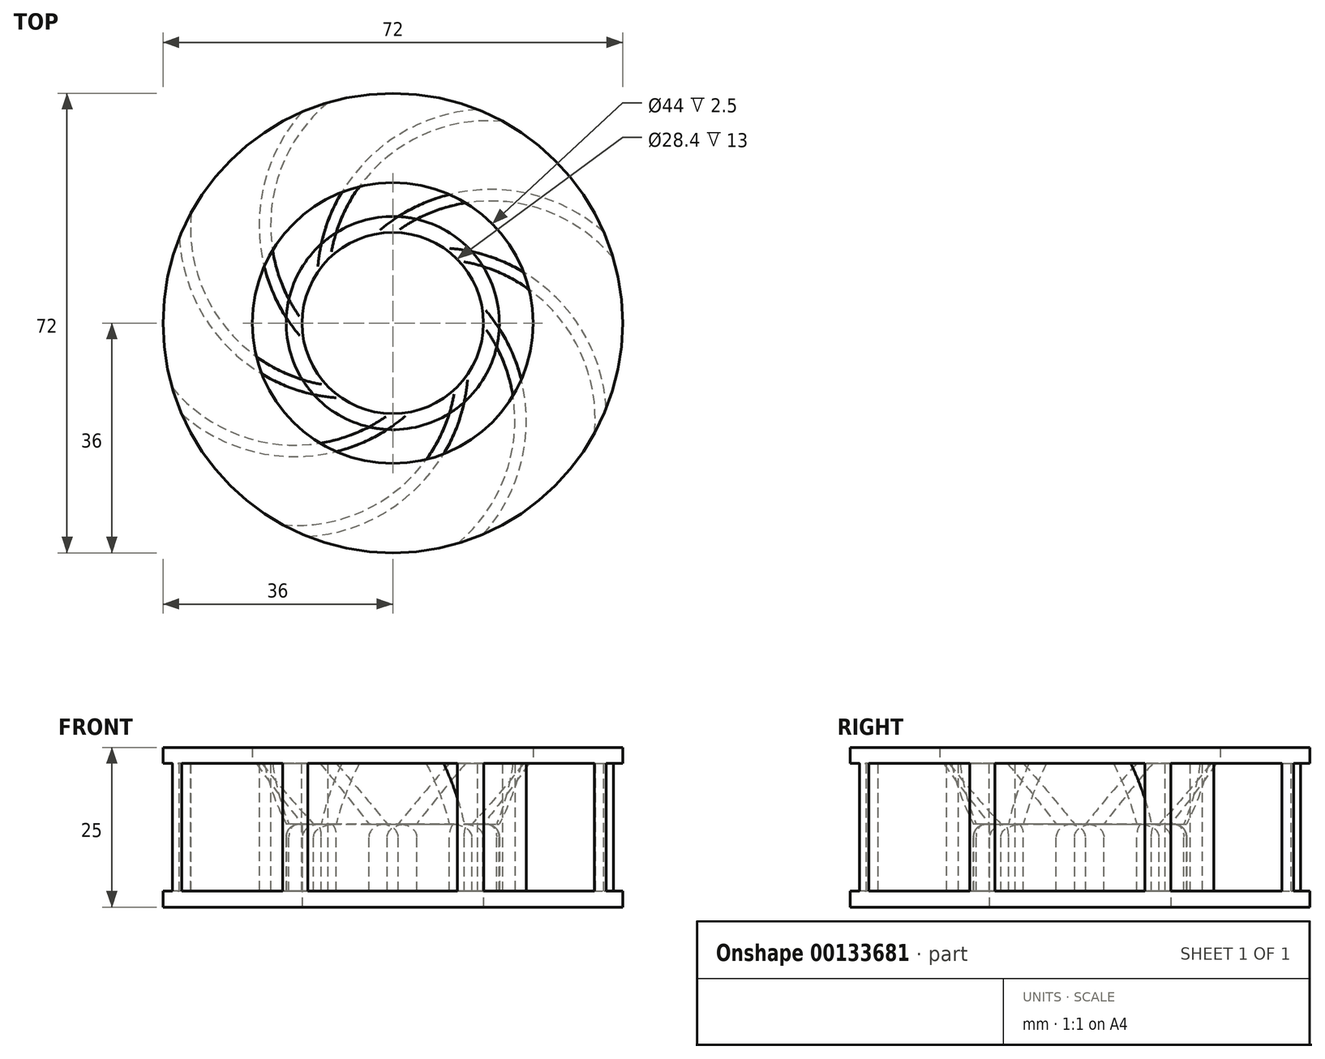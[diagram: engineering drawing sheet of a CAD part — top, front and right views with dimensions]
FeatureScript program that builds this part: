
annotation { "Feature Type Name" : "Feature", "Feature Type Description" : "" }
export const myFeature = defineFeature(function(context is Context, id is Id, definition is map)
    precondition{}
    {
        {
            var Q0;
            Q0=qCreatedBy(makeId("Top.planeOp"),FACE);
            var sketch = newSketch(context, id + "F0", { "sketchPlane" : qUnion([Q0])});
            skCircle(sketch, "E0", {"center": v(0, 0) * mm, "radius": 38 * mm});
            skCircle(sketch, "E1", {"center": v(0, 0) * mm, "radius": 14 * mm, "construction": true});
            skCircle(sketch, "E2", {"center": v(-5, 15) * mm, "radius": 25 * mm});
            skCircle(sketch, "E3", {"center": v(-5, 15) * mm, "radius": 26.8 * mm});
            skLineSegment(sketch, "E4", {"start": v(-5, 15) * mm, "end": v(0, 15) * mm});
            skLineSegment(sketch, "E5", {"start": v(0, 15) * mm, "end": v(0, 0) * mm});
            skLineSegment(sketch, "E6", {"start": v(-2.4, -9.86) * mm, "end": v(5, -9.86) * mm});
            skSolve(sketch);
        }
        {
            var Q0;
            {var subQ0=sQuery(id+"F0.wireOp",EDGE,"E3");var subQ1=sQuery(id+"F0.wireOp",EDGE,"E0");var subQ2=makeQuery(id+"F0.imprint","INTERSECT",VERTEX,{"disambiguationData":[OD(1.0)],"derivedFrom":[subQ1,subQ0]});Q0=makeQuery(id+"F0.imprint","IMPRINT",FACE,{"disambiguationData":[TD([[makeQuery(id+"F0.imprint","IMPRINT",EDGE,{"disambiguationData":[TD([[subQ2,1.0]])],"derivedFrom":subQ1}),1.0]])]});}
            var Q1;
            {var subQ0=sQuery(id+"F0.wireOp",EDGE,"E6");Q1=makeQuery(id+"F0.imprint","IMPRINT",FACE,{"disambiguationData":[TD([[makeQuery(id+"F0.imprint","IMPRINT",EDGE,{"derivedFrom":subQ0}),-1.0]])]});}
            var Q2;
            {var subQ5=sQuery(id+"F0.wireOp",EDGE,"E6");Q2=makeQuery(id+"F0.imprint","IMPRINT",FACE,{"disambiguationData":[TD([[makeQuery(id+"F0.imprint","IMPRINT",EDGE,{"derivedFrom":subQ5}),1.0]])]});}
            var Q3;
            {var subQ0=sQuery(id+"F0.wireOp",EDGE,"E3");var subQ1=sQuery(id+"F0.wireOp",EDGE,"E0");var subQ2=makeQuery(id+"F0.imprint","INTERSECT",VERTEX,{"disambiguationData":[OD(0.0)],"derivedFrom":[subQ1,subQ0]});Q3=makeQuery(id+"F0.imprint","IMPRINT",FACE,{"disambiguationData":[TD([[makeQuery(id+"F0.imprint","IMPRINT",EDGE,{"disambiguationData":[TD([[subQ2,-1.0]])],"derivedFrom":subQ1}),-1.0]])]});}
            extrude(context, id + "F1", {"entities" : qUnion([Q0, Q1, Q2, Q3]), "endBound" : BoundingType.SYMMETRIC, "depth" : 80 * mm});
        }
        {
            var Q0;
            Q0=qCreatedBy(makeId("Front.planeOp"),FACE);
            var sketch = newSketch(context, id + "F2", { "sketchPlane" : qUnion([Q0])});
            skLineSegment(sketch, "E7", {"start": v(0, 0) * mm, "end": v(0, 0) * mm});
            skLineSegment(sketch, "E8", {"start": v(36, 2.5) * mm, "end": v(36, 22.5) * mm});
            skLineSegment(sketch, "E9", {"start": v(36, 25) * mm, "end": v(36, 22.5) * mm});
            skLineSegment(sketch, "E10", {"start": v(36, 2.5) * mm, "end": v(36, 0) * mm});
            skLineSegment(sketch, "E11", {"start": v(14.2, 0) * mm, "end": v(14.2, 2.5) * mm});
            skLineSegment(sketch, "E12", {"start": v(22, 22.5) * mm, "end": v(22, 25) * mm});
            skLineSegment(sketch, "E13", {"start": v(36, 22.5) * mm, "end": v(22, 22.5) * mm});
            skLineSegment(sketch, "E14", {"start": v(14.2, 0) * mm, "end": v(0, 0) * mm});
            skLineSegment(sketch, "E15", {"start": v(36, 25) * mm, "end": v(22, 25) * mm});
            skLineSegment(sketch, "E16", {"start": v(0, 0) * mm, "end": v(0, 37.29) * mm, "construction": true});
            skLineSegment(sketch, "E17", {"start": v(14.2, 0) * mm, "end": v(36, 0) * mm});
            skLineSegment(sketch, "E18", {"start": v(36, 2.5) * mm, "end": v(14.2, 2.5) * mm});
            skLineSegment(sketch, "E19", {"start": v(14.2, 2.5) * mm, "end": v(14.2, 13) * mm});
            skLineSegment(sketch, "E20", {"start": v(14.2, 13) * mm, "end": v(16.7, 13) * mm});
            skLineSegment(sketch, "E21", {"start": v(16.7, 13) * mm, "end": v(16.7, 2.5) * mm});
            skLineSegment(sketch, "E22", {"start": v(16.7, 13) * mm, "end": v(22, 22.5) * mm});
            skSolve(sketch);
        }
        {
            var Q0;
            Q0=makeQuery(id+"F1.opExtrude","SWEPT_BODY",BODY,{"disambiguationData":[OSD([sQuery(id+"F0.wireOp",EDGE,"E2"),sQuery(id+"F0.wireOp",EDGE,"E3")])]});
            transform(context, id + "F3", {"entities" : qUnion([Q0]), "transformType" : TransformType.TRANSLATION_3D, "dx" : -1.7 * mm, "dy" : 0 * mm, "dz" : 0 * mm, "makeCopy" : false});
        }
        {
            var Q0;
            Q0=makeQuery(id+"F2.imprint","IMPRINT",FACE,{"disambiguationData":[TD([[makeQuery(id+"F2.imprint","IMPRINT",EDGE,{"derivedFrom":sQuery(id+"F2.wireOp",EDGE,"E8")}),1.0]])]});
            var Q1;
            Q1=sQuery(id+"F2.wireOp",EDGE,"E16");
            revolve(context, id + "F4", {"operationType" : NewBodyOperationType.INTERSECT, "entities" : qUnion([Q0]), "axis" : qUnion([Q1]), "revolveType" : RevolveType.ONE_DIRECTION, "oppositeDirection" : true, "angle" : 210 * degree});
        }
        {
            var Q0;
            {var subQ0=sQuery(id+"F2.wireOp",EDGE,"E19");Q0=makeQuery(id+"F2.imprint","IMPRINT",FACE,{"disambiguationData":[TD([[makeQuery(id+"F2.imprint","IMPRINT",EDGE,{"derivedFrom":subQ0}),-1.0]])]});}
            var Q1;
            {var subQ1=sQuery(id+"F2.wireOp",EDGE,"E10");Q1=makeQuery(id+"F2.imprint","IMPRINT",FACE,{"disambiguationData":[TD([[makeQuery(id+"F2.imprint","IMPRINT",EDGE,{"derivedFrom":subQ1}),-1.0]])]});}
            var Q2;
            Q2=makeQuery(id+"F2.imprint","IMPRINT",FACE,{"disambiguationData":[TD([[makeQuery(id+"F2.imprint","IMPRINT",EDGE,{"derivedFrom":sQuery(id+"F2.wireOp",EDGE,"E9")}),-1.0]])]});
            var Q3;
            Q3=sQuery(id+"F2.wireOp",EDGE,"E16");
            revolve(context, id + "F5", {"entities" : qUnion([Q0, Q1, Q2]), "axis" : qUnion([Q3]), "revolveType" : RevolveType.FULL});
        }
        {
            var Q0;
            Q0=makeQuery(id+"F1.opExtrude","SWEPT_BODY",BODY,{"disambiguationData":[OSD([sQuery(id+"F0.wireOp",EDGE,"E2"),sQuery(id+"F0.wireOp",EDGE,"E3")])]});
            var Q1;
            Q1=sQuery(id+"F2.wireOp",EDGE,"E16");
            var Q2;
            Q2=makeQuery(id+"F5.opRevolve","SWEPT_BODY",BODY,{"disambiguationData":[OSD([sQuery(id+"F2.wireOp",EDGE,"3ec203e2-959f-4f1b-bf71-badd138a0934.0"),sQuery(id+"F2.wireOp",EDGE,"E9"),sQuery(id+"F2.wireOp",EDGE,"E12"),sQuery(id+"F2.wireOp",EDGE,"E13")])]});
            var Q3;
            Q3=makeQuery(id+"F5.opRevolve","SWEPT_BODY",BODY,{"disambiguationData":[OSD([sQuery(id+"F2.wireOp",EDGE,"qKgDXYYX-TTP8-Qoq3-12mj-SkwD0XB7USGg"),sQuery(id+"F2.wireOp",EDGE,"JF4CM9u2-8K3e-R4AF-DxyI-4FNlkfHP6lGW"),sQuery(id+"F2.wireOp",EDGE,"ODSA0SzI-IWFj-hovR-A0oM-EIshQltW2pC4"),sQuery(id+"F2.wireOp",EDGE,"vagTDOvN-KNsH-OysZ-BbLi-oJHE3Bp00F4F")])]});
            var Q4;
            Q4=makeQuery(id+"F5.opRevolve","SWEPT_BODY",BODY,{"disambiguationData":[OSD([sQuery(id+"F2.wireOp",EDGE,"E10"),sQuery(id+"F2.wireOp",EDGE,"E11"),sQuery(id+"F2.wireOp",EDGE,"igcslDpy-jmUK-c8h7-VBtI-GKYrrJpq7DNQ"),sQuery(id+"F2.wireOp",EDGE,"YB9619NM-3txE-2ZHe-G0ve-K0Xd8lPiis2H"),sQuery(id+"F2.wireOp",EDGE,"Bw529zTH-jyWE-afGY-0HaI-DwoyFS4O8YbO"),sQuery(id+"F2.wireOp",EDGE,"0wlXGYjg-B1NC-aLFa-TOcu-qfCg6hhzO9Te"),sQuery(id+"F2.wireOp",EDGE,"iNVBEw9w-Od8l-R6Ku-DCX1-71FtL8oE5t7T"),sQuery(id+"F2.wireOp",EDGE,"PiUjfzoK-myfQ-hyxR-wMBp-s5GPztHALuDE")])]});
            circularPattern(context, id + "F6", {"operationType" : NewBodyOperationType.ADD, "entities" : qUnion([Q0]), "axis" : qUnion([Q1]), "angle" : 45 * degree, "instanceCount" : 8});
        }
        {
            var Q0;
            {var subQ0=sQuery(id+"F2.wireOp",EDGE,"E22");var subQ2=sQuery(id+"F2.wireOp",EDGE,"E21");var subQ3=sQuery(id+"F2.wireOp",EDGE,"E20");Q0=makeQuery(id+"F6.boolean.opBoolean","SPLIT",EDGE,{"disambiguationData":[TD([makeQuery(id+"F6.opPattern","COPY",FACE,{"derivedFrom":makeQuery(id+"F1.opExtrude","SWEPT_FACE",FACE,{"disambiguationData":[OSD([sQuery(id+"F0.wireOp",EDGE,"E3")])]}),"instanceName":"3"})])],"derivedFrom":makeQuery(id+"F5.opRevolve","SWEPT_EDGE",EDGE,{"disambiguationData":[OSD([subQ3,subQ2,subQ0])]})});}
            var Q1;
            {var subQ0=sQuery(id+"F2.wireOp",EDGE,"E21");var subQ1=sQuery(id+"F2.wireOp",EDGE,"E22");var subQ3=sQuery(id+"F2.wireOp",EDGE,"E20");Q1=makeQuery(id+"F6.boolean.opBoolean","SPLIT",EDGE,{"disambiguationData":[TD([makeQuery(id+"F6.opPattern","COPY",FACE,{"derivedFrom":makeQuery(id+"F1.opExtrude","SWEPT_FACE",FACE,{"disambiguationData":[OSD([sQuery(id+"F0.wireOp",EDGE,"E3")])]}),"instanceName":"2"})])],"derivedFrom":makeQuery(id+"F5.opRevolve","SWEPT_EDGE",EDGE,{"disambiguationData":[OSD([subQ3,subQ0,subQ1])]})});}
            var Q2;
            {var subQ0=sQuery(id+"F2.wireOp",EDGE,"E21");var subQ1=sQuery(id+"F2.wireOp",EDGE,"E22");var subQ3=sQuery(id+"F2.wireOp",EDGE,"E20");Q2=makeQuery(id+"F6.boolean.opBoolean","SPLIT",EDGE,{"disambiguationData":[TD([makeQuery(id+"F6.opPattern","COPY",FACE,{"derivedFrom":makeQuery(id+"F1.opExtrude","SWEPT_FACE",FACE,{"disambiguationData":[OSD([sQuery(id+"F0.wireOp",EDGE,"E3")])]}),"instanceName":"1"})])],"derivedFrom":makeQuery(id+"F5.opRevolve","SWEPT_EDGE",EDGE,{"disambiguationData":[OSD([subQ3,subQ0,subQ1])]})});}
            var Q3;
            {var subQ0=sQuery(id+"F2.wireOp",EDGE,"E21");var subQ1=sQuery(id+"F2.wireOp",EDGE,"E20");var subQ2=sQuery(id+"F2.wireOp",EDGE,"E22");Q3=makeQuery(id+"F6.boolean.opBoolean","SPLIT",EDGE,{"disambiguationData":[TD([makeQuery(id+"F1.opExtrude","SWEPT_FACE",FACE,{"disambiguationData":[OSD([sQuery(id+"F0.wireOp",EDGE,"E3")])]})])],"derivedFrom":makeQuery(id+"F5.opRevolve","SWEPT_EDGE",EDGE,{"disambiguationData":[OSD([subQ1,subQ0,subQ2])]})});}
            var Q4;
            {var subQ0=sQuery(id+"F2.wireOp",EDGE,"E20");var subQ1=sQuery(id+"F2.wireOp",EDGE,"E22");var subQ3=sQuery(id+"F2.wireOp",EDGE,"E21");Q4=makeQuery(id+"F6.boolean.opBoolean","SPLIT",EDGE,{"disambiguationData":[TD([makeQuery(id+"F1.opExtrude","SWEPT_FACE",FACE,{"disambiguationData":[OSD([sQuery(id+"F0.wireOp",EDGE,"E2")])]})])],"derivedFrom":makeQuery(id+"F5.opRevolve","SWEPT_EDGE",EDGE,{"disambiguationData":[OSD([subQ0,subQ3,subQ1])]})});}
            var Q5;
            {var subQ0=sQuery(id+"F2.wireOp",EDGE,"E22");var subQ2=sQuery(id+"F2.wireOp",EDGE,"E21");var subQ3=sQuery(id+"F2.wireOp",EDGE,"E20");Q5=makeQuery(id+"F6.boolean.opBoolean","SPLIT",EDGE,{"disambiguationData":[TD([makeQuery(id+"F6.opPattern","COPY",FACE,{"derivedFrom":makeQuery(id+"F1.opExtrude","SWEPT_FACE",FACE,{"disambiguationData":[OSD([sQuery(id+"F0.wireOp",EDGE,"E3")])]}),"instanceName":"6"})])],"derivedFrom":makeQuery(id+"F5.opRevolve","SWEPT_EDGE",EDGE,{"disambiguationData":[OSD([subQ3,subQ2,subQ0])]})});}
            var Q6;
            {var subQ0=sQuery(id+"F2.wireOp",EDGE,"E22");var subQ2=sQuery(id+"F2.wireOp",EDGE,"E20");var subQ3=sQuery(id+"F2.wireOp",EDGE,"E21");Q6=makeQuery(id+"F6.boolean.opBoolean","SPLIT",EDGE,{"disambiguationData":[TD([makeQuery(id+"F6.opPattern","COPY",FACE,{"derivedFrom":makeQuery(id+"F1.opExtrude","SWEPT_FACE",FACE,{"disambiguationData":[OSD([sQuery(id+"F0.wireOp",EDGE,"E3")])]}),"instanceName":"5"})])],"derivedFrom":makeQuery(id+"F5.opRevolve","SWEPT_EDGE",EDGE,{"disambiguationData":[OSD([subQ2,subQ3,subQ0])]})});}
            var Q7;
            {var subQ0=sQuery(id+"F2.wireOp",EDGE,"E21");var subQ1=sQuery(id+"F2.wireOp",EDGE,"E22");var subQ3=sQuery(id+"F2.wireOp",EDGE,"E20");Q7=makeQuery(id+"F6.boolean.opBoolean","SPLIT",EDGE,{"disambiguationData":[TD([makeQuery(id+"F6.opPattern","COPY",FACE,{"derivedFrom":makeQuery(id+"F1.opExtrude","SWEPT_FACE",FACE,{"disambiguationData":[OSD([sQuery(id+"F0.wireOp",EDGE,"E3")])]}),"instanceName":"4"})])],"derivedFrom":makeQuery(id+"F5.opRevolve","SWEPT_EDGE",EDGE,{"disambiguationData":[OSD([subQ3,subQ0,subQ1])]})});}
            fillet(context, id + "F7", {"entities" : qUnion([Q0, Q1, Q2, Q3, Q4, Q5, Q6, Q7]), "radius" : 2 * mm, "tangentPropagation" : true, "allowEdgeOverflow" : false});
        }
    });
